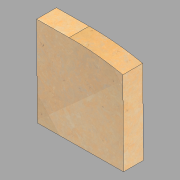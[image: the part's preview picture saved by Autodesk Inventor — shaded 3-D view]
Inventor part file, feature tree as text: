
AUTODESK INVENTOR PART (.ipt)
format: ipt  version: 2022.1 (Build 261234020, 234B)  size: 112,128 bytes
history: imported  units: in
note: dims shown in document units (in); Inventor stores cm internally (conversion verified against a paired STEP export)
features: imported_body x1
ambient origin geometry x8: Origin, YZ Plane, XZ Plane, XY Plane, X Axis, Y Axis, Z Axis, Center Point
bodies: Solid1 (imported_parasolid)
feature tree (1):
  imported_body  NMx_Import_Brep_tag  [imported B-rep: ~7 faces, bbox_mm=[666.359512, 687.953551, 152.4]]
